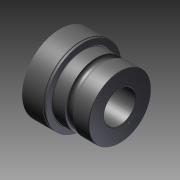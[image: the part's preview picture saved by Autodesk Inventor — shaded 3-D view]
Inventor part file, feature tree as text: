
AUTODESK INVENTOR PART (.ipt)
format: ipt  version: 2016 (Build 200138000, 138)  size: 230,912 bytes
history: native  units: mm
features: other x7, revolve x1, sketch x1
ambient origin geometry x8: Origin, YZ Plane, XZ Plane, XY Plane, X Axis, Y Axis, Z Axis, Center Point
bodies: Solid1 (feature_tree)
feature tree (9):
  revolve  "Revolution1"  [1 undecoded]
  other  "to_housing_XY"
  other  "to_housing_YZ"
  other  "to_housing_ZX"
  other  "to_housing_X"
  other  "to_housing_Y"
  other  "to_housing_Z"
  other  "to_housing_Center"
  sketch  "Sketch_1"  dims[d0=360.0deg d1=0.0mm]
note: 1 required parameter value undecoded (feature->parameter linkage not recoverable at this tier; creation-order binding heuristic only, values carry confidence <= 0.55)
